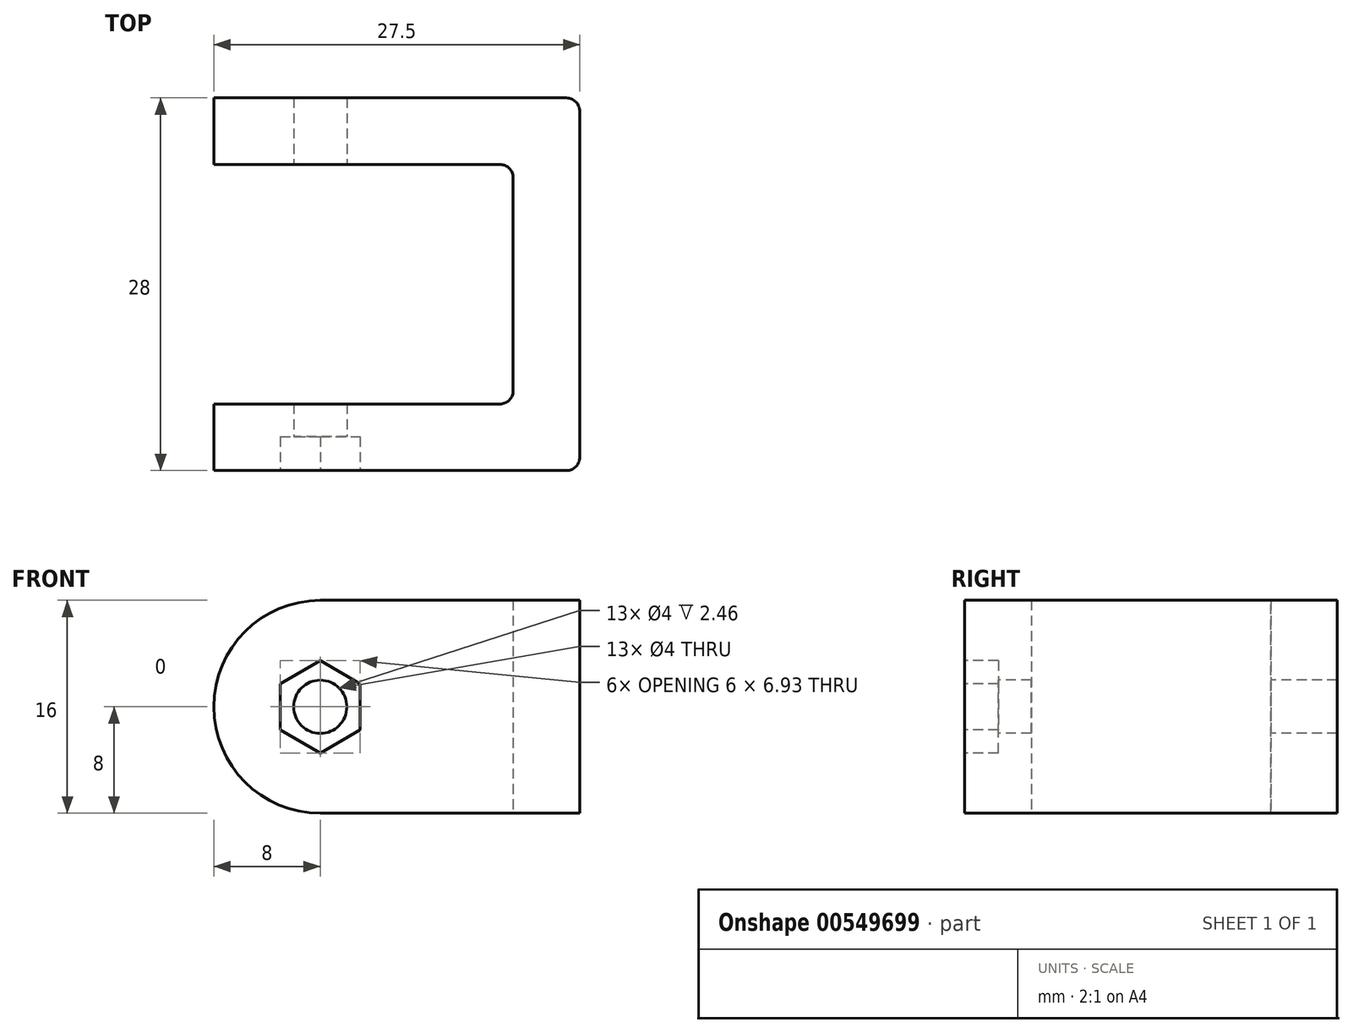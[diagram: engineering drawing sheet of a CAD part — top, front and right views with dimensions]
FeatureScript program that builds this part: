
annotation { "Feature Type Name" : "Feature", "Feature Type Description" : "" }
export const myFeature = defineFeature(function(context is Context, id is Id, definition is map)
    precondition{}
    {
        {
            var Q0;
            Q0=qCreatedBy(makeId("Top.planeOp"),FACE);
            var sketch = newSketch(context, id + "F0", { "sketchPlane" : qUnion([Q0])});
            skLineSegment(sketch, "E0", {"start": v(0, 18) * mm, "end": v(22.5, 18) * mm});
            skLineSegment(sketch, "E1", {"start": v(22.5, 18) * mm, "end": v(22.5, 0) * mm});
            skLineSegment(sketch, "E2", {"start": v(22.5, 0) * mm, "end": v(0, 0) * mm});
            skLineSegment(sketch, "E3.0", {"start": v(27.5, -5) * mm, "end": v(0, -5) * mm});
            skLineSegment(sketch, "E3.1", {"start": v(27.5, 23) * mm, "end": v(27.5, -5) * mm});
            skLineSegment(sketch, "E3.2", {"start": v(0, 23) * mm, "end": v(27.5, 23) * mm});
            skLineSegment(sketch, "E4", {"start": v(0, 23) * mm, "end": v(0, 18) * mm});
            skLineSegment(sketch, "E5", {"start": v(0, -5) * mm, "end": v(0, 0) * mm});
            skSolve(sketch);
        }
        {
            var Q0;
            Q0 = qSketchRegion(id + "F0", true);
            extrude(context, id + "F1", {"entities" : qUnion([Q0]), "depth" : 16 * mm, "offsetDistance" : 25 * mm});
        }
        {
            var Q0;
            Q0=makeQuery(id+"F1.opExtrude","SWEPT_FACE",FACE,{"disambiguationData":[OSD([sQuery(id+"F0.wireOp",EDGE,"E3.0")])]});
            var sketch = newSketch(context, id + "F2", { "sketchPlane" : qUnion([Q0])});
            skLineSegment(sketch, "E6", {"start": v(0, 8) * mm, "end": v(27.5, 8) * mm, "construction": true});
            skPoint(sketch, "E7", {"position": v(8, 8) * mm});
            skCircle(sketch, "E8.cCircle", {"center": v(8, 8) * mm, "radius": 3 * mm, "construction": true});
            skLineSegment(sketch, "E8.0", {"start": v(11, 9.73) * mm, "end": v(11, 6.27) * mm});
            skLineSegment(sketch, "E8.1", {"start": v(11, 6.27) * mm, "end": v(8, 4.54) * mm});
            skLineSegment(sketch, "E8.2", {"start": v(8, 4.54) * mm, "end": v(5, 6.27) * mm});
            skLineSegment(sketch, "E8.3", {"start": v(5, 6.27) * mm, "end": v(5, 9.73) * mm});
            skLineSegment(sketch, "E8.4", {"start": v(5, 9.73) * mm, "end": v(8, 11.46) * mm});
            skLineSegment(sketch, "E8.5", {"start": v(8, 11.46) * mm, "end": v(11, 9.73) * mm});
            skPoint(sketch, "E8.0.midPoint", {"position": v(11, 8) * mm});
            skSolve(sketch);
        }
        {
            var Q0;
            Q0=sQuery(id+"F2.wireOp",VERTEX,"E7");
            var Q1;
            Q1=makeQuery(id+"F1.opExtrude","SWEPT_BODY",BODY,{"disambiguationData":[OSD([sQuery(id+"F0.wireOp",EDGE,"E0"),sQuery(id+"F0.wireOp",EDGE,"E1"),sQuery(id+"F0.wireOp",EDGE,"E2"),sQuery(id+"F0.wireOp",EDGE,"E3.0"),sQuery(id+"F0.wireOp",EDGE,"E3.1"),sQuery(id+"F0.wireOp",EDGE,"E3.2"),sQuery(id+"F0.wireOp",EDGE,"E4"),sQuery(id+"F0.wireOp",EDGE,"E5")])]});
            hole(context, id + "F3", {"style" : HoleStyle.SIMPLE, "endStyle" : HoleEndStyle.BLIND, "holeDiameter" : 4 * mm, "holeDepth" : 30 * mm, "isTappedThrough" : true, "tappedDepth" : 12 * mm, "tapClearance" : 3, "startFromSketch" : true, "locations" : qUnion([Q0]), "scope" : qUnion([Q1])});
        }
        {
            var Q0;
            Q0=makeQuery(id+"F1.opExtrude","SWEPT_EDGE",EDGE,{"disambiguationData":[OSD([sQuery(id+"F0.wireOp",EDGE,"E0"),sQuery(id+"F0.wireOp",EDGE,"E1")])]});
            var Q1;
            Q1=makeQuery(id+"F1.opExtrude","SWEPT_EDGE",EDGE,{"disambiguationData":[OSD([sQuery(id+"F0.wireOp",EDGE,"E1"),sQuery(id+"F0.wireOp",EDGE,"E2")])]});
            var Q2;
            Q2=makeQuery(id+"F1.opExtrude","SWEPT_EDGE",EDGE,{"disambiguationData":[OSD([sQuery(id+"F0.wireOp",EDGE,"E3.0"),sQuery(id+"F0.wireOp",EDGE,"E3.1")])]});
            var Q3;
            Q3=makeQuery(id+"F1.opExtrude","SWEPT_EDGE",EDGE,{"disambiguationData":[OSD([sQuery(id+"F0.wireOp",EDGE,"E3.1"),sQuery(id+"F0.wireOp",EDGE,"E3.2")])]});
            fillet(context, id + "F4", {"entities" : qUnion([Q0, Q1, Q2, Q3]), "radius" : 1 * mm, "tangentPropagation" : true, "allowEdgeOverflow" : false});
        }
        {
            var Q0;
            Q0=makeQuery(id+"F1.opExtrude","CAP_EDGE",EDGE,{"disambiguationData":[OSD([sQuery(id+"F0.wireOp",EDGE,"E5")])],"isStart":false});
            var Q1;
            Q1=makeQuery(id+"F1.opExtrude","CAP_EDGE",EDGE,{"disambiguationData":[OSD([sQuery(id+"F0.wireOp",EDGE,"E4")])],"isStart":false});
            var Q2;
            Q2=makeQuery(id+"F1.opExtrude","CAP_EDGE",EDGE,{"disambiguationData":[OSD([sQuery(id+"F0.wireOp",EDGE,"E5")])],"isStart":true});
            var Q3;
            Q3=makeQuery(id+"F1.opExtrude","CAP_EDGE",EDGE,{"disambiguationData":[OSD([sQuery(id+"F0.wireOp",EDGE,"E4")])],"isStart":true});
            fillet(context, id + "F5", {"entities" : qUnion([Q0, Q1, Q2, Q3]), "radius" : 8 * mm, "tangentPropagation" : true, "allowEdgeOverflow" : false});
        }
        {
            var Q0;
            Q0=makeQuery(id+"F2.imprint","IMPRINT",FACE,{"disambiguationData":[TD([[makeQuery(id+"F2.imprint","IMPRINT",EDGE,{"derivedFrom":sQuery(id+"F2.wireOp",EDGE,"E8.0")}),-1.0]])]});
            extrude(context, id + "F6", {"entities" : qUnion([Q0]), "operationType" : NewBodyOperationType.REMOVE, "oppositeDirection" : true, "depth" : 2.54 * mm, "offsetDistance" : 25 * mm});
        }
    });
